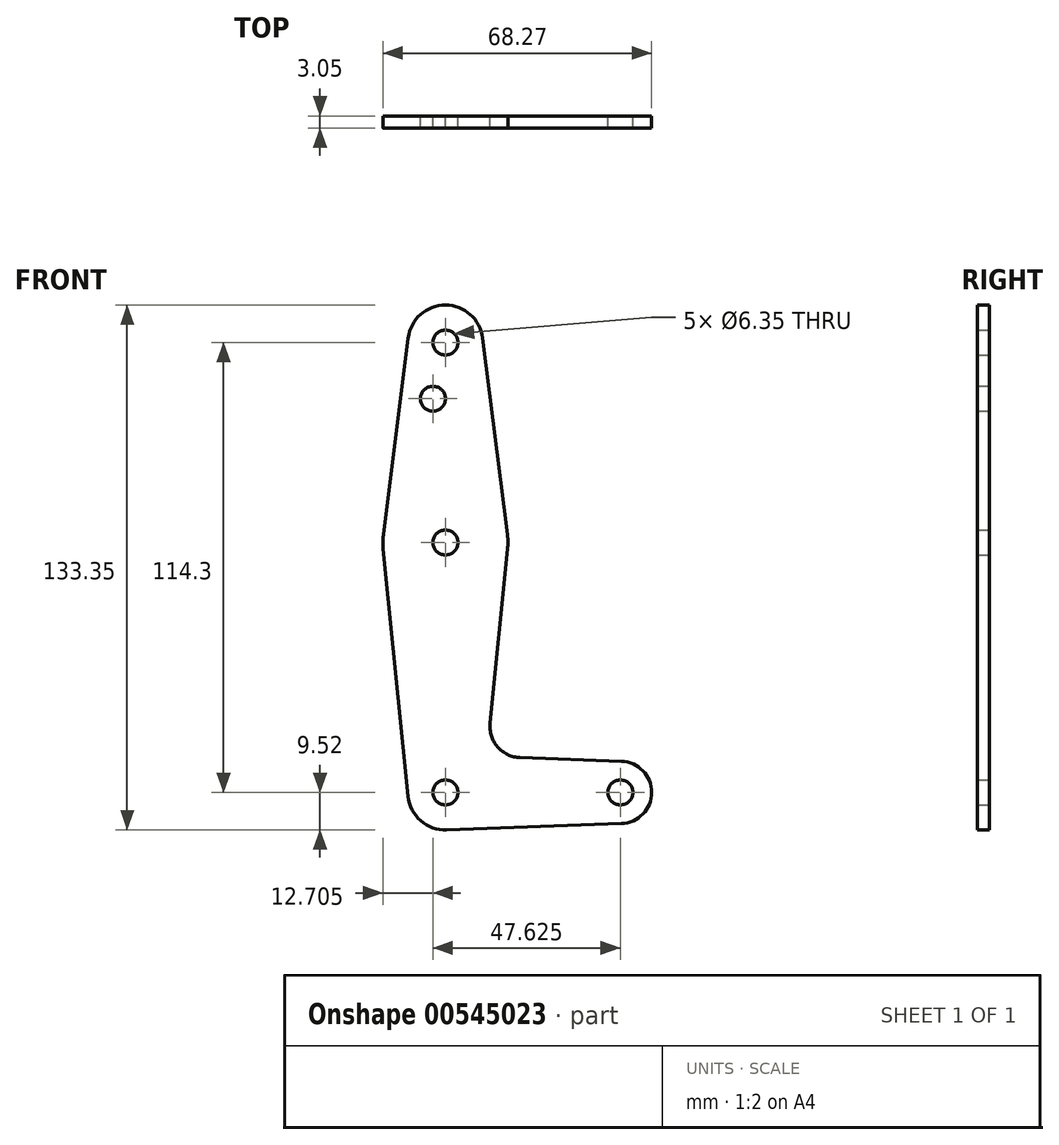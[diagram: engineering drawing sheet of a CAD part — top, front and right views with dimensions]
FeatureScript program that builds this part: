
annotation { "Feature Type Name" : "Feature", "Feature Type Description" : "" }
export const myFeature = defineFeature(function(context is Context, id is Id, definition is map)
    precondition{}
    {
        {
            var Q0;
            Q0=qCreatedBy(makeId("Front.planeOp"),FACE);
            var sketch = newSketch(context, id + "F0", { "sketchPlane" : qUnion([Q0])});
            skLineSegment(sketch, "E0", {"start": v(0, 0) * mm, "end": v(0, 114.3) * mm, "construction": true});
            skLineSegment(sketch, "E1", {"start": v(0, 0) * mm, "end": v(44.45, 0) * mm, "construction": true});
            skCircle(sketch, "E2", {"center": v(0, 0) * mm, "radius": 9.53 * mm});
            skCircle(sketch, "E3", {"center": v(0, 114.3) * mm, "radius": 9.53 * mm});
            skCircle(sketch, "E4", {"center": v(44.45, 0) * mm, "radius": 7.94 * mm});
            skCircle(sketch, "E5", {"center": v(0, 63.5) * mm, "radius": 15.88 * mm});
            skLineSegment(sketch, "E6", {"start": v(-15.75, 65.48) * mm, "end": v(-9.45, 115.5) * mm});
            skLineSegment(sketch, "E7", {"start": v(9.45, 115.5) * mm, "end": v(15.75, 65.48) * mm});
            skLineSegment(sketch, "E8", {"start": v(-15.8, 61.91) * mm, "end": v(-9.48, -0.95) * mm});
            skLineSegment(sketch, "E9", {"start": v(44.73, -7.93) * mm, "end": v(0, -9.53) * mm});
            skCircle(sketch, "E10", {"center": v(0, 114.3) * mm, "radius": 3.18 * mm});
            skCircle(sketch, "E11", {"center": v(0, 63.5) * mm, "radius": 3.18 * mm});
            skCircle(sketch, "E12", {"center": v(0, 0) * mm, "radius": 3.18 * mm});
            skCircle(sketch, "E13", {"center": v(44.45, 0) * mm, "radius": 3.18 * mm});
            skCircle(sketch, "E14", {"center": v(-3.18, 100.03) * mm, "radius": 3.18 * mm});
            skLineSegment(sketch, "E15", {"start": v(15.8, 61.91) * mm, "end": v(11.34, 17.6) * mm});
            skLineSegment(sketch, "E16", {"start": v(44.73, 7.93) * mm, "end": v(18.97, 8.85) * mm});
            skArc(sketch, "E17.filletArc", {"start": v(11.34, 17.6) * mm, "mid": v(13.26, 11.57) * mm, "end": v(18.97, 8.85) * mm});
            skSolve(sketch);
        }
        {
            var Q0;
            Q0 = qSketchRegion(id + "F0", true);
            extrude(context, id + "F1", {"entities" : qUnion([Q0]), "depth" : 3.05 * mm, "offsetDistance" : 25 * mm});
        }
    });
